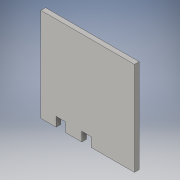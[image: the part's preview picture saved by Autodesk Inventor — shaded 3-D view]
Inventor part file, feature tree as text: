
AUTODESK INVENTOR PART (.ipt)
format: ipt  version: 2016 (Build 200138000, 138)  size: 105,472 bytes
history: native  units: in
note: dims shown in document units (in); Inventor stores cm internally (conversion verified against a paired STEP export)
features: extrude x1, sketch x1
ambient origin geometry x8: Origin, YZ Plane, XZ Plane, XY Plane, X Axis, Y Axis, Z Axis, Center Point
bodies: Solid1 (feature_tree)
feature tree (2):
  extrude  "Extrusion1"  Depth=10.0in
  sketch  "Sketch1"  dims[d0=10.0in d1=10.0in d2=3.5in d3=1.0in d4=1.0in d5=1.0in d6=0.875in d7=0.875in d8=0.5in d9=0.0in]
